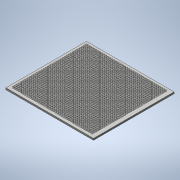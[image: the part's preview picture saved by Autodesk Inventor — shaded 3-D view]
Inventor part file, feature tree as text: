
AUTODESK INVENTOR PART (.ipt)
format: ipt  version: 2022 (Build 260153000, 153)  size: 6,505,472 bytes
history: native  units: in
note: dims shown in document units (in); Inventor stores cm internally (conversion verified against a paired STEP export)
features: extrude x2, sketch x2
ambient origin geometry x8: Origin, YZ Plane, XZ Plane, XY Plane, X Axis, Y Axis, Z Axis, Center Point
bodies: Solid1 (feature_tree)
feature tree (4):
  extrude  "Extrusion1"  Depth=1.811in
  extrude  "Extrusion3"  Depth=0.0217in
  sketch  "Sketch1"  dims[d0=1.9685in d1=1.811in]
  sketch  "Sketch3"  dims[d2=0.0394in d3=0.0in d17=0.0217in d18=0.0217in d19=0.0787in d20=0.0787in d21=16.5354in d23=0.0433in d24=15.3543in d26=0.0433in d29=0.0315in d30=0.0in]
